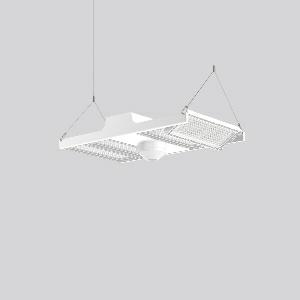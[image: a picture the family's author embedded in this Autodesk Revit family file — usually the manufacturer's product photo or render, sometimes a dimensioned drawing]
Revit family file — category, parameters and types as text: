
# Revit family: light_case_sensor_921692_002_76_2a28
name_source: partatom
category: Lighting Fixtures
units: mm (PartAtom-declared; Revit-internal decimal feet)

## family parameters
Cut with Voids When Loaded = No
Host = Face
Light Source = No
Part Type = Normal
Room Calculation Point = No
Round Connector Dimension = Use Diameter
Shared = No

## types (1)
- LIGHT CASE SENSOR (1 x LED Modul 840, 8900 lm, 4000)
    Apparent Load = 225 VA
    CIE Flux Codes = 81 98 100 100 100
    Color Rendering = 80
    Color Temperature = 4000
    Default Elevation = 1800 mm
    Description = Series: LIGHT CASE SENSOR
Flat highbay luminaire for chain or cable suspension with 4 LED modules that can be swivelled. Housing: die cast aluminium and sheet steel, powder-coated. Optimised thermal management thanks to special luminaire design. Self-cleaning heat sink for constant heat dissipation. Cover: plastic (polycarbonate, shockproof), with integrated four-row lens system. LED modules can be swivelled ± 30° for optimum illumination. Suitable for chain or steel cable suspension (to be provided on site). With 5-pin connection terminal (1.5 m). Built-in DALI sensor for daylight- and presence-dependent lighting control. Light and presence sensor: Housing: plastic. Functions can be used separately. 2 DALI input addresses. Detection range: 18 m. Light sensor range: 20-800 lx (measured at the sensor). Installation height: up to 13 m. Example of use: Walking motion detection of persons: 3-10 m installation height. Vehicle motion detector (e.g. fork lift): 3-13 m installation height. Luminaire with limited surface temperature in accordance with EN 60598-2-24 for use in environments in which a deposit of conductive dust on the luminaire can be expected. 
Colour: white
Length: 680 mm
Width: 397 mm
Height: 187 mm
Lamp: LED
Socket: without socket
Colour temperature: 4000K
Colour rendering index (CRI): 80
System power: 225 W
Rated luminous flux: 35600 lm
Luminous efficiency: 158 lm/W
Control gear: Converter, dimmable, DALI
Protection class: I
Type of protection: IP 54
    Height = 187 mm
    Lamp = 1 x LED Modul 840
    Lamp Light Flux = 8900 lm
    Lamp count = 1
    Length = 680 mm
    Lifetime = 50000 h
    Luminous efficacy = 158 lm/W
    Manufacturer = RZB
    ModVariant = No
    Model = 921692.002.76
    Mounting Place = Ceiling
    Mounting Type = Pendant
    Number of Poles = 1
    OnlyDefault = Yes
    Power Factor = 1
    Product Name = LIGHT CASE SENSOR
    Product group = Pendant commercial luminaires
    ProductGroupID = 903
    Protection Class = Protection class I
    Protection Degree = IP 65
    RLX_Detail_Level = 1
    RLX_Emergency_Light_Flux = 0 lm
    RLX_Emergency_Type = 0
    RLX_Emergency_Type_DB = No
    RlxData = <blob elided: 27453 chars, md5=8c40d777>
    Socket = socket
    Standby Power = 0 W
    System Light Flux = 35600 lm
    System Power = 225 W
    Type Comments = Product without accessories
    Type Image = 921528.002.76.jpg
    URL = http://relux.com
    VarID = ---
    Voltage = 230 V
    Voltage Range = 220-240 V
    Weight = 0.00 kg
    Width = 397 mm

## geometry (parser evidence)
native form markers: Blend x4, Sweep x22
no freeform markers — native parametric forms only
